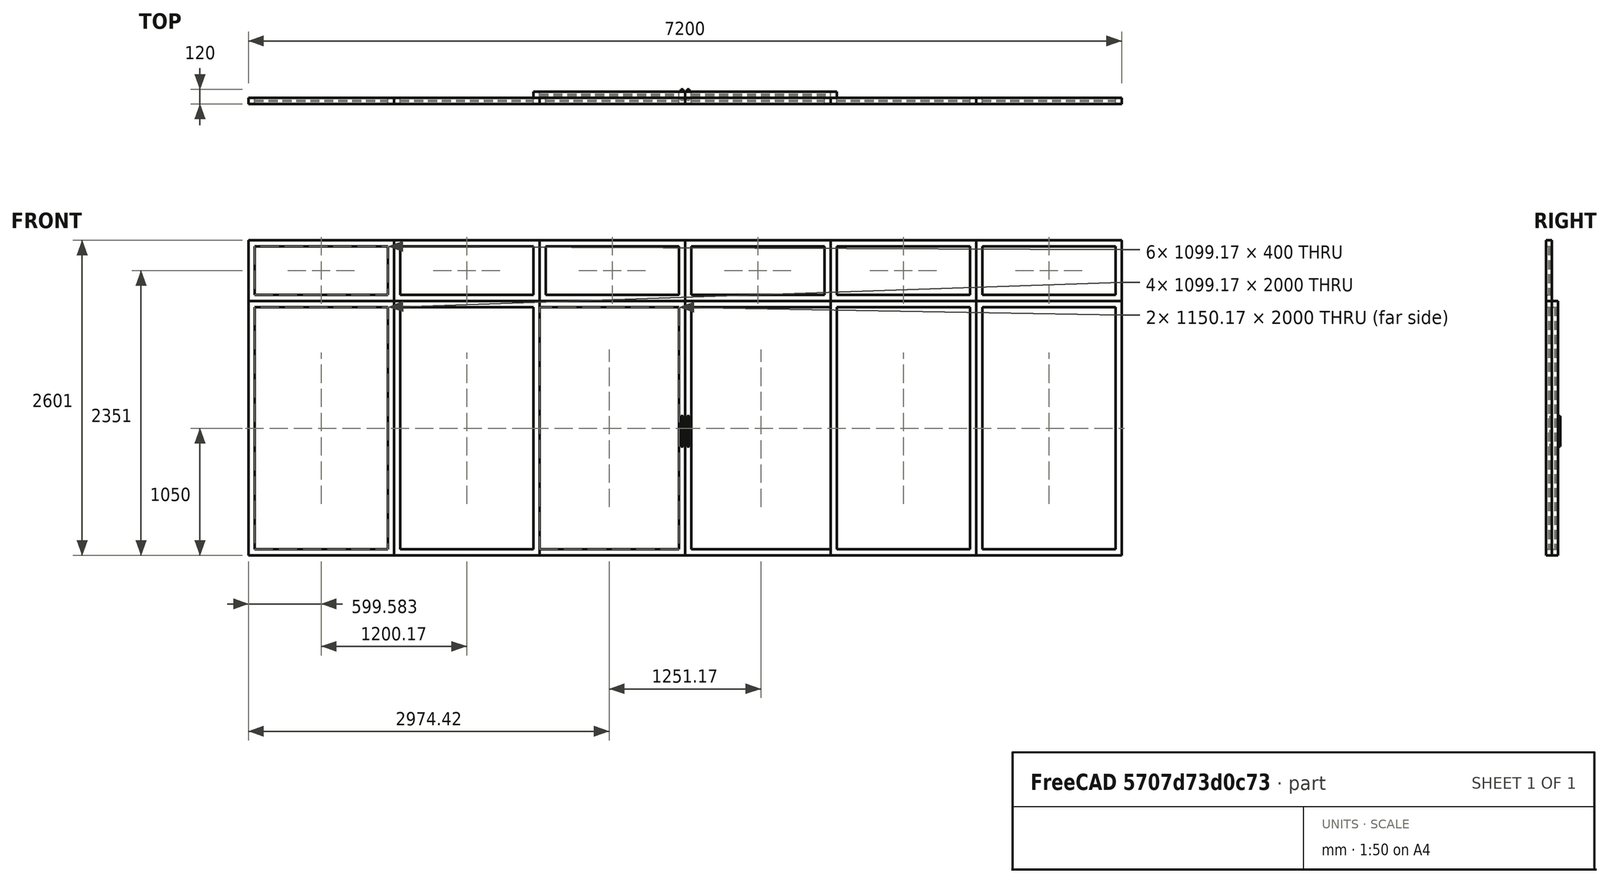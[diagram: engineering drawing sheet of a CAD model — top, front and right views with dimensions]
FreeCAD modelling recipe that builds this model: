
FCSTD DOCUMENT  (FreeCAD 0.16R6704 (Git))
Label: 6 frame modules with doors
License: CreativeCommons Attribution
LicenseURL: http://creativecommons.org/licenses/by/4.0/
objects: Sketcher::SketchObject×1, Part::FeaturePython×1
note: 2 computed .brp shape members not serialized (recipe doc carries the construction recipe); baked Part::Feature solids carry a one-line shape summary decoded from their .brp

FEATURE [Sketcher::SketchObject] Sketch190
  Placement = pos=(0,0,0) rot=(1,0,0;1.5708rad)
  sketch-geometry (135):
    g0: LineSegment StartX=-2 StartY=-2 StartZ=0 EndX=7202 EndY=-2 EndZ=0
    g1: LineSegment StartX=7202 StartY=-2 StartZ=0 EndX=7202 EndY=2603 EndZ=0
    g2: LineSegment StartX=7202 StartY=2603 StartZ=0 EndX=-2 EndY=2603 EndZ=0
    g3: LineSegment StartX=-2 StartY=2603 StartZ=0 EndX=-2 EndY=-2 EndZ=0
    g4: LineSegment StartX=0 StartY=2601 StartZ=0 EndX=1199.17 EndY=2601 EndZ=0
    g5: LineSegment StartX=1199.17 StartY=2601 StartZ=0 EndX=1199.17 EndY=2101 EndZ=0
    g6: LineSegment StartX=1199.17 StartY=2101 StartZ=0 EndX=0 EndY=2101 EndZ=0
    g7: LineSegment StartX=0 StartY=2101 StartZ=0 EndX=0 EndY=2601 EndZ=0
    g8: LineSegment StartX=50 StartY=2551 StartZ=0 EndX=1149.17 EndY=2551 EndZ=0
    g9: LineSegment StartX=1149.17 StartY=2551 StartZ=0 EndX=1149.17 EndY=2151 EndZ=0
    g10: LineSegment StartX=1149.17 StartY=2151 StartZ=0 EndX=50 EndY=2151 EndZ=0
    g11: LineSegment StartX=50 StartY=2151 StartZ=0 EndX=50 EndY=2551 EndZ=0
    g12: LineSegment StartX=0 StartY=2100 StartZ=0 EndX=1199.17 EndY=2100 EndZ=0
    g13: LineSegment StartX=1199.17 StartY=2100 StartZ=0 EndX=1199.17 EndY=0 EndZ=0
    g14: LineSegment StartX=1199.17 StartY=0 StartZ=0 EndX=0 EndY=0 EndZ=0
    g15: LineSegment StartX=0 StartY=0 StartZ=0 EndX=0 EndY=2100 EndZ=0
    g16: LineSegment StartX=50 StartY=2050 StartZ=0 EndX=1149.17 EndY=2050 EndZ=0
    g17: LineSegment StartX=1149.17 StartY=2050 StartZ=0 EndX=1149.17 EndY=50 EndZ=0
    g18: LineSegment StartX=1149.17 StartY=50 StartZ=0 EndX=50 EndY=50 EndZ=0
    g19: LineSegment StartX=50 StartY=50 StartZ=0 EndX=50 EndY=2050 EndZ=0
    g20: LineSegment StartX=-1 StartY=2602 StartZ=0 EndX=7201 EndY=2602 EndZ=0
    g21: LineSegment StartX=7201 StartY=2602 StartZ=0 EndX=7201 EndY=-1 EndZ=0
    g22: LineSegment StartX=7201 StartY=-1 StartZ=0 EndX=-1 EndY=-1 EndZ=0
    g23: LineSegment StartX=-1 StartY=-1 StartZ=0 EndX=-1 EndY=2602 EndZ=0
    g24: LineSegment StartX=1200.17 StartY=2601 StartZ=0 EndX=2399.33 EndY=2601 EndZ=0
    g25: LineSegment StartX=2399.33 StartY=2601 StartZ=0 EndX=2399.33 EndY=2101 EndZ=0
    g26: LineSegment StartX=2399.33 StartY=2101 StartZ=0 EndX=1200.17 EndY=2101 EndZ=0
    g27: LineSegment StartX=1200.17 StartY=2101 StartZ=0 EndX=1200.17 EndY=2601 EndZ=0
    g28: LineSegment StartX=1250.17 StartY=2551 StartZ=0 EndX=2349.33 EndY=2551 EndZ=0
    g29: LineSegment StartX=2349.33 StartY=2551 StartZ=0 EndX=2349.33 EndY=2151 EndZ=0
    g30: LineSegment StartX=2349.33 StartY=2151 StartZ=0 EndX=1250.17 EndY=2151 EndZ=0
    g31: LineSegment StartX=1250.17 StartY=2151 StartZ=0 EndX=1250.17 EndY=2551 EndZ=0
    g32: LineSegment StartX=1200.17 StartY=2100 StartZ=0 EndX=2399.33 EndY=2100 EndZ=0
    g33: LineSegment StartX=2399.33 StartY=2100 StartZ=0 EndX=2399.33 EndY=0 EndZ=0
    g34: LineSegment StartX=2399.33 StartY=0 StartZ=0 EndX=1200.17 EndY=0 EndZ=0
    g35: LineSegment StartX=1200.17 StartY=0 StartZ=0 EndX=1200.17 EndY=2100 EndZ=0
    g36: LineSegment StartX=1250.17 StartY=2050 StartZ=0 EndX=2349.33 EndY=2050 EndZ=0
    g37: LineSegment StartX=2349.33 StartY=2050 StartZ=0 EndX=2349.33 EndY=50 EndZ=0
    g38: LineSegment StartX=2349.33 StartY=50 StartZ=0 EndX=1250.17 EndY=50 EndZ=0
    g39: LineSegment StartX=1250.17 StartY=50 StartZ=0 EndX=1250.17 EndY=2050 EndZ=0
    g40: LineSegment [constr] StartX=0 StartY=2601 StartZ=0 EndX=1200.17 EndY=2601 EndZ=0
    g41: LineSegment StartX=2400.33 StartY=2601 StartZ=0 EndX=3599.5 EndY=2601 EndZ=0
    g42: LineSegment StartX=3599.5 StartY=2601 StartZ=0 EndX=3599.5 EndY=2101 EndZ=0
    g43: LineSegment StartX=3599.5 StartY=2101 StartZ=0 EndX=2400.33 EndY=2101 EndZ=0
    g44: LineSegment StartX=2400.33 StartY=2101 StartZ=0 EndX=2400.33 EndY=2601 EndZ=0
    g45: LineSegment StartX=2450.33 StartY=2551 StartZ=0 EndX=3549.5 EndY=2551 EndZ=0
    g46: LineSegment StartX=3549.5 StartY=2551 StartZ=0 EndX=3549.5 EndY=2151 EndZ=0
    g47: LineSegment StartX=3549.5 StartY=2151 StartZ=0 EndX=2450.33 EndY=2151 EndZ=0
    g48: LineSegment StartX=2450.33 StartY=2151 StartZ=0 EndX=2450.33 EndY=2551 EndZ=0
    g49: LineSegment StartX=2349.33 StartY=2100 StartZ=0 EndX=3599.5 EndY=2100 EndZ=0
    g50: LineSegment StartX=3599.5 StartY=2100 StartZ=0 EndX=3599.5 EndY=0 EndZ=0
    g51: LineSegment StartX=3599.5 StartY=0 StartZ=0 EndX=2349.33 EndY=0 EndZ=0
    g52: LineSegment StartX=2349.33 StartY=0 StartZ=0 EndX=2349.33 EndY=2100 EndZ=0
    g53: LineSegment StartX=2399.33 StartY=2050 StartZ=0 EndX=3549.5 EndY=2050 EndZ=0
    g54: LineSegment StartX=3549.5 StartY=2050 StartZ=0 EndX=3549.5 EndY=50 EndZ=0
    g55: LineSegment StartX=3549.5 StartY=50 StartZ=0 EndX=2399.33 EndY=50 EndZ=0
    g56: LineSegment StartX=2399.33 StartY=50 StartZ=0 EndX=2399.33 EndY=2050 EndZ=0
    g57: LineSegment [constr] StartX=1200.17 StartY=2601 StartZ=0 EndX=2400.33 EndY=2601 EndZ=0
    g58: LineSegment StartX=3600.5 StartY=2601 StartZ=0 EndX=4799.67 EndY=2601 EndZ=0
    g59: LineSegment StartX=4799.67 StartY=2601 StartZ=0 EndX=4799.67 EndY=2101 EndZ=0
    g60: LineSegment StartX=4799.67 StartY=2101 StartZ=0 EndX=3600.5 EndY=2101 EndZ=0
    g61: LineSegment StartX=3600.5 StartY=2101 StartZ=0 EndX=3600.5 EndY=2601 EndZ=0
    g62: LineSegment StartX=3650.5 StartY=2551 StartZ=0 EndX=4749.67 EndY=2551 EndZ=0
    g63: LineSegment StartX=4749.67 StartY=2551 StartZ=0 EndX=4749.67 EndY=2151 EndZ=0
    g64: LineSegment StartX=4749.67 StartY=2151 StartZ=0 EndX=3650.5 EndY=2151 EndZ=0
    g65: LineSegment StartX=3650.5 StartY=2151 StartZ=0 EndX=3650.5 EndY=2551 EndZ=0
    g66: LineSegment StartX=3600.5 StartY=2100 StartZ=0 EndX=4850.67 EndY=2100 EndZ=0
    g67: LineSegment StartX=4850.67 StartY=2100 StartZ=0 EndX=4850.67 EndY=0 EndZ=0
    g68: LineSegment StartX=4850.67 StartY=0 StartZ=0 EndX=3600.5 EndY=0 EndZ=0
    g69: LineSegment StartX=3600.5 StartY=0 StartZ=0 EndX=3600.5 EndY=2100 EndZ=0
    g70: LineSegment StartX=3650.5 StartY=2050 StartZ=0 EndX=4800.67 EndY=2050 EndZ=0
    g71: LineSegment StartX=4800.67 StartY=2050 StartZ=0 EndX=4800.67 EndY=50 EndZ=0
    g72: LineSegment StartX=4800.67 StartY=50 StartZ=0 EndX=3650.5 EndY=50 EndZ=0
    g73: LineSegment StartX=3650.5 StartY=50 StartZ=0 EndX=3650.5 EndY=2050 EndZ=0
    g74: LineSegment [constr] StartX=2400.33 StartY=2601 StartZ=0 EndX=3600.5 EndY=2601 EndZ=0
    g75: LineSegment StartX=4800.67 StartY=2601 StartZ=0 EndX=5999.83 EndY=2601 EndZ=0
    g76: LineSegment StartX=5999.83 StartY=2601 StartZ=0 EndX=5999.83 EndY=2101 EndZ=0
    g77: LineSegment StartX=5999.83 StartY=2101 StartZ=0 EndX=4800.67 EndY=2101 EndZ=0
    g78: LineSegment StartX=4800.67 StartY=2101 StartZ=0 EndX=4800.67 EndY=2601 EndZ=0
    g79: LineSegment StartX=4850.67 StartY=2551 StartZ=0 EndX=5949.83 EndY=2551 EndZ=0
    g80: LineSegment StartX=5949.83 StartY=2551 StartZ=0 EndX=5949.83 EndY=2151 EndZ=0
    g81: LineSegment StartX=5949.83 StartY=2151 StartZ=0 EndX=4850.67 EndY=2151 EndZ=0
    g82: LineSegment StartX=4850.67 StartY=2151 StartZ=0 EndX=4850.67 EndY=2551 EndZ=0
    g83: LineSegment StartX=4800.67 StartY=2100 StartZ=0 EndX=5999.83 EndY=2100 EndZ=0
    g84: LineSegment StartX=5999.83 StartY=2100 StartZ=0 EndX=5999.83 EndY=0 EndZ=0
    g85: LineSegment StartX=5999.83 StartY=0 StartZ=0 EndX=4800.67 EndY=0 EndZ=0
    g86: LineSegment StartX=4800.67 StartY=0 StartZ=0 EndX=4800.67 EndY=2100 EndZ=0
    g87: LineSegment StartX=4850.67 StartY=2050 StartZ=0 EndX=5949.83 EndY=2050 EndZ=0
    g88: LineSegment StartX=5949.83 StartY=2050 StartZ=0 EndX=5949.83 EndY=50 EndZ=0
    g89: LineSegment StartX=5949.83 StartY=50 StartZ=0 EndX=4850.67 EndY=50 EndZ=0
    g90: LineSegment StartX=4850.67 StartY=50 StartZ=0 EndX=4850.67 EndY=2050 EndZ=0
    g91: LineSegment [constr] StartX=3600.5 StartY=2601 StartZ=0 EndX=4800.67 EndY=2601 EndZ=0
    g92: LineSegment StartX=6000.83 StartY=2601 StartZ=0 EndX=7200 EndY=2601 EndZ=0
    g93: LineSegment StartX=7200 StartY=2601 StartZ=0 EndX=7200 EndY=2101 EndZ=0
    g94: LineSegment StartX=7200 StartY=2101 StartZ=0 EndX=6000.83 EndY=2101 EndZ=0
    g95: LineSegment StartX=6000.83 StartY=2101 StartZ=0 EndX=6000.83 EndY=2601 EndZ=0
    g96: LineSegment StartX=6050.83 StartY=2551 StartZ=0 EndX=7150 EndY=2551 EndZ=0
    g97: LineSegment StartX=7150 StartY=2551 StartZ=0 EndX=7150 EndY=2151 EndZ=0
    g98: LineSegment StartX=7150 StartY=2151 StartZ=0 EndX=6050.83 EndY=2151 EndZ=0
    g99: LineSegment StartX=6050.83 StartY=2151 StartZ=0 EndX=6050.83 EndY=2551 EndZ=0
    g100: LineSegment StartX=6000.83 StartY=2100 StartZ=0 EndX=7200 EndY=2100 EndZ=0
    g101: LineSegment StartX=7200 StartY=2100 StartZ=0 EndX=7200 EndY=0 EndZ=0
    g102: LineSegment StartX=7200 StartY=0 StartZ=0 EndX=6000.83 EndY=0 EndZ=0
    g103: LineSegment StartX=6000.83 StartY=0 StartZ=0 EndX=6000.83 EndY=2100 EndZ=0
    g104: LineSegment StartX=6050.83 StartY=2050 StartZ=0 EndX=7150 EndY=2050 EndZ=0
    g105: LineSegment StartX=7150 StartY=2050 StartZ=0 EndX=7150 EndY=50 EndZ=0
    g106: LineSegment StartX=7150 StartY=50 StartZ=0 EndX=6050.83 EndY=50 EndZ=0
    g107: LineSegment StartX=6050.83 StartY=50 StartZ=0 EndX=6050.83 EndY=2050 EndZ=0
    g108: LineSegment [constr] StartX=4800.67 StartY=2601 StartZ=0 EndX=6000.83 EndY=2601 EndZ=0
    g109: LineSegment StartX=3564.5 StartY=1150 StartZ=0 EndX=3584.5 EndY=1150 EndZ=0
    g110: LineSegment StartX=3584.5 StartY=1150 StartZ=0 EndX=3584.5 EndY=900 EndZ=0
    g111: LineSegment StartX=3584.5 StartY=900 StartZ=0 EndX=3564.5 EndY=900 EndZ=0
    g112: LineSegment StartX=3564.5 StartY=900 StartZ=0 EndX=3564.5 EndY=1150 EndZ=0
    g113: LineSegment StartX=3615.5 StartY=1150 StartZ=0 EndX=3635.5 EndY=1150 EndZ=0
    g114: LineSegment StartX=3635.5 StartY=1150 StartZ=0 EndX=3635.5 EndY=900 EndZ=0
    g115: LineSegment StartX=3635.5 StartY=900 StartZ=0 EndX=3615.5 EndY=900 EndZ=0
    g116: LineSegment StartX=3615.5 StartY=900 StartZ=0 EndX=3615.5 EndY=1150 EndZ=0
    g117: LineSegment [constr] StartX=60.6664 StartY=50 StartZ=0 EndX=60.6664 EndY=0 EndZ=0
    g118: LineSegment [constr] StartX=0 StartY=2393.34 StartZ=0 EndX=50 EndY=2393.34 EndZ=0
    g119: LineSegment [constr] StartX=141.741 StartY=2601 StartZ=0 EndX=141.741 EndY=2551 EndZ=0
    g120: LineSegment [constr] StartX=1149.17 StartY=2527.5 StartZ=0 EndX=1199.17 EndY=2527.5 EndZ=0
    g121: LineSegment [constr] StartX=1200.17 StartY=2516.49 StartZ=0 EndX=1250.17 EndY=2516.49 EndZ=0
    g122: LineSegment [constr] StartX=2349.33 StartY=2495 StartZ=0 EndX=2399.33 EndY=2495 EndZ=0
    g123: LineSegment [constr] StartX=2400.33 StartY=2493.39 StartZ=0 EndX=2450.33 EndY=2493.39 EndZ=0
    g124: LineSegment [constr] StartX=3549.5 StartY=2542 StartZ=0 EndX=3599.5 EndY=2542 EndZ=0
    g125: LineSegment [constr] StartX=3600.5 StartY=2538 StartZ=0 EndX=3650.5 EndY=2538 EndZ=0
    g126: LineSegment [constr] StartX=4749.67 StartY=2530.45 StartZ=0 EndX=4799.67 EndY=2530.45 EndZ=0
    g127: LineSegment [constr] StartX=4800.67 StartY=2534.58 StartZ=0 EndX=4850.67 EndY=2534.58 EndZ=0
    g128: LineSegment [constr] StartX=5949.83 StartY=2532.69 StartZ=0 EndX=5999.83 EndY=2532.69 EndZ=0
    g129: LineSegment [constr] StartX=6000.83 StartY=2528 StartZ=0 EndX=6050.83 EndY=2528 EndZ=0
    g130: LineSegment [constr] StartX=7150 StartY=2521.34 StartZ=0 EndX=7200 EndY=2521.34 EndZ=0
    g131: LineSegment [constr] StartX=28.9872 StartY=2151 StartZ=0 EndX=28.9872 EndY=2101 EndZ=0
    g132: LineSegment [constr] StartX=57.4326 StartY=2100 StartZ=0 EndX=57.4326 EndY=2050 EndZ=0
    g133: LineSegment [constr] StartX=3584.5 StartY=1150 StartZ=0 EndX=3599.5 EndY=1150 EndZ=0
    g134: LineSegment [constr] StartX=3615.5 StartY=1150 StartZ=0 EndX=3600.5 EndY=1150 EndZ=0
  constraints (399):
    c: Coincident(g0,g1)
    c: Coincident(g1,g2)
    c: Coincident(g2,g3)
    c: Coincident(g3,g0)
    c: Horizontal(g0)
    c: Horizontal(g2)
    c: Vertical(g1)
    c: Vertical(g3)
    c: Coincident(g4,g5)
    c: Coincident(g5,g6)
    c: Coincident(g6,g7)
    c: Coincident(g7,g4)
    c: Horizontal(g4)
    c: Horizontal(g6)
    c: Vertical(g5)
    c: Vertical(g7)
    c: Coincident(g8,g9)
    c: Coincident(g9,g10)
    c: Coincident(g10,g11)
    c: Coincident(g11,g8)
    c: Horizontal(g8)
    c: Horizontal(g10)
    c: Vertical(g9)
    c: Vertical(g11)
    c: Coincident(g12,g13)
    c: Coincident(g13,g14)
    c: Coincident(g14,g15)
    c: Coincident(g15,g12)
    c: Horizontal(g12)
    c: Horizontal(g14)
    c: Vertical(g13)
    c: Vertical(g15)
    c: Coincident(g16,g17)
    c: Coincident(g17,g18)
    c: Coincident(g18,g19)
    c: Coincident(g19,g16)
    c: Horizontal(g16)
    c: Horizontal(g18)
    c: Vertical(g17)
    c: Vertical(g19)
    c: Coincident(g20,g21)
    c: Coincident(g21,g22)
    c: Coincident(g22,g23)
    c: Coincident(g23,g20)
    c: Horizontal(g20)
    c: Horizontal(g22)
    c: Vertical(g21)
    c: Vertical(g23)
    c: DistanceX(g2,g20) = 1  'Largura do marco vertical 1 geral'
    c: DistanceY(g20,g2) = 1  'Altura do marco geral'
    c: DistanceX(g20,g4) = 1
    c: DistanceY(g4,g20) = 1
    c: DistanceX(g22,g14) = 1
    c: DistanceY(g22,g14) = 1
    c: DistanceY(g12,g6) = 1
    c: DistanceX(g4,g8) = 50  'Dimensão perfis'
    c: Coincident(g14,g-1)  'Constraint58'
    c: DistanceY(g-1,g12) = 2100  'Altura portas e perfis'
    c: DistanceY(g6,g4) = 500  'Altura bandeira'
    c: Coincident(g24,g25)  'Constraint60'
    c: Coincident(g25,g26)
    c: Coincident(g26,g27)
    c: Coincident(g27,g24)
    c: Horizontal(g24)
    c: Horizontal(g26)
    c: Vertical(g25)
    c: Vertical(g27)
    c: Coincident(g28,g29)
    c: Coincident(g29,g30)
    c: Coincident(g30,g31)
    c: Coincident(g31,g28)
    c: Horizontal(g28)
    c: Horizontal(g30)
    c: Vertical(g29)
    c: Vertical(g31)
    c: Coincident(g32,g33)
    c: Coincident(g33,g34)
    c: Coincident(g34,g35)
    c: Coincident(g35,g32)
    c: Horizontal(g32)
    c: Horizontal(g34)
    c: Vertical(g33)
    c: Vertical(g35)
    c: Coincident(g36,g37)
    c: Coincident(g37,g38)
    c: Coincident(g38,g39)
    c: Coincident(g39,g36)
    c: Horizontal(g36)
    c: Horizontal(g38)
    c: Vertical(g37)
    c: Vertical(g39)
    c: Equal(g4,g24) = 1199
    c: Coincident(g4,g40)
    c: Coincident(g24,g40)
    c: Angle(g40) = 0
    c: Coincident(g41,g42)
    c: Coincident(g42,g43)
    c: Coincident(g43,g44)
    c: Coincident(g44,g41)
    c: Horizontal(g41)
    c: Horizontal(g43)
    c: Vertical(g42)
    c: Vertical(g44)
    c: Coincident(g45,g46)
    c: Coincident(g46,g47)
    c: Coincident(g47,g48)
    c: Coincident(g48,g45)
    c: Horizontal(g45)
    c: Horizontal(g47)
    c: Vertical(g46)
    c: Vertical(g48)
    c: Coincident(g49,g50)
    c: Coincident(g50,g51)
    c: Coincident(g51,g52)
    c: Coincident(g52,g49)
    c: Horizontal(g49)
    c: Horizontal(g51)
    c: Vertical(g50)
    c: Vertical(g52)
    c: Coincident(g53,g54)
    c: Coincident(g54,g55)
    c: Coincident(g55,g56)
    c: Coincident(g56,g53)
    c: Horizontal(g53)
    c: Horizontal(g55)
    c: Vertical(g54)
    c: Vertical(g56)
    c: Equal(g4,g41) = 1199
    c: Coincident(g24,g57)
    c: Coincident(g41,g57)
    c: Equal(g40,g57)
    c: Parallel(g57,g40)
    c: Coincident(g58,g59)
    c: Coincident(g59,g60)
    c: Coincident(g60,g61)
    c: Coincident(g61,g58)
    c: Horizontal(g58)
    c: Horizontal(g60)
    c: Vertical(g59)
    c: Vertical(g61)
    c: Coincident(g62,g63)
    c: Coincident(g63,g64)
    c: Coincident(g64,g65)
    c: Coincident(g65,g62)
    c: Horizontal(g62)
    c: Horizontal(g64)
    c: Vertical(g63)
    c: Vertical(g65)
    c: Coincident(g66,g67)
    c: Coincident(g67,g68)
    c: Coincident(g68,g69)
    c: Coincident(g69,g66)
    c: Horizontal(g66)
    c: Horizontal(g68)
    c: Vertical(g67)
    c: Vertical(g69)
    c: Coincident(g70,g71)
    c: Coincident(g71,g72)
    c: Coincident(g72,g73)
    c: Coincident(g73,g70)
    c: Horizontal(g70)
    c: Horizontal(g72)
    c: Vertical(g71)
    c: Vertical(g73)
    c: Equal(g4,g58) = 1199
    c: Coincident(g41,g74)
    c: Coincident(g58,g74)
    c: Equal(g40,g74)
    c: Parallel(g74,g40)
    c: Coincident(g75,g76)
    c: Coincident(g76,g77)
    c: Coincident(g77,g78)
    c: Coincident(g78,g75)
    c: Horizontal(g75)
    c: Horizontal(g77)
    c: Vertical(g76)
    c: Vertical(g78)
    c: Coincident(g79,g80)
    c: Coincident(g80,g81)
    c: Coincident(g81,g82)
    c: Coincident(g82,g79)
    c: Horizontal(g79)
    c: Horizontal(g81)
    c: Vertical(g80)
    c: Vertical(g82)
    c: Coincident(g83,g84)
    c: Coincident(g84,g85)
    c: Coincident(g85,g86)
    c: Coincident(g86,g83)
    c: Horizontal(g83)
    c: Horizontal(g85)
    c: Vertical(g84)
    c: Vertical(g86)
    c: Coincident(g87,g88)
    c: Coincident(g88,g89)
    c: Coincident(g89,g90)
    c: Coincident(g90,g87)
    c: Horizontal(g87)
    c: Horizontal(g89)
    c: Vertical(g88)
    c: Vertical(g90)
    c: Equal(g4,g75) = 1199
    c: Coincident(g58,g91)
    c: Coincident(g75,g91)
    c: Equal(g40,g91)
    c: Parallel(g91,g40)
    c: Coincident(g92,g93)
    c: Coincident(g93,g94)
    c: Coincident(g94,g95)
    c: Coincident(g95,g92)
    c: Horizontal(g92)
    c: Horizontal(g94)
    c: Vertical(g93)
    c: Vertical(g95)
    c: Coincident(g96,g97)
    c: Coincident(g97,g98)
    c: Coincident(g98,g99)
    c: Coincident(g99,g96)
    c: Horizontal(g96)
    c: Horizontal(g98)
    c: Vertical(g97)
    c: Vertical(g99)
    c: Coincident(g100,g101)
    c: Coincident(g101,g102)
    c: Coincident(g102,g103)
    c: Coincident(g103,g100)
    c: Horizontal(g100)
    c: Horizontal(g102)
    c: Vertical(g101)
    c: Vertical(g103)
    c: Coincident(g104,g105)
    c: Coincident(g105,g106)
    c: Coincident(g106,g107)
    c: Coincident(g107,g104)
    c: Horizontal(g104)
    c: Horizontal(g106)
    c: Vertical(g105)
    c: Vertical(g107)
    c: Equal(g4,g92) = 1199
    c: Coincident(g75,g108)
    c: Coincident(g92,g108)
    c: Equal(g40,g108)
    c: Parallel(g108,g40)
    c: Coincident(g109,g110)
    c: Coincident(g110,g111)
    c: Coincident(g111,g112)
    c: Coincident(g112,g109)
    c: Horizontal(g109)
    c: Horizontal(g111)
    c: Vertical(g110)
    c: Vertical(g112)
    c: Coincident(g113,g114)
    c: Coincident(g114,g115)
    c: Coincident(g115,g116)
    c: Coincident(g116,g113)
    c: Horizontal(g113)
    c: Horizontal(g115)
    c: Vertical(g114)
    c: Vertical(g116)
    c: DistanceY(g110,g115) = 0
    c: DistanceY(g113,g109) = 0
    c: DistanceX(g109,g109) = 20  'Largura puxadores'
    c: DistanceX(g26,g32) = 0  'Constraint263'
    c: DistanceX(g36,g29) = 0
    c: DistanceX(g36,g49) = 0
    c: DistanceX(g42,g49) = 0
    c: DistanceX(g60,g66) = 0
    c: DistanceX(g87,g81) = 0
    c: DistanceX(g66,g87) = 0
    c: DistanceX(g76,g83) = 0
    c: DistanceX(g94,g100) = 0
    c: DistanceX(g93,g100) = 0
    c: DistanceX(g-1,g101) = 7200  'Largura do vão'
    c: DistanceY(g8,g28) = 0  'Constraint280'
    c: DistanceY(g28,g45) = 0  'Constraint278'
    c: DistanceY(g45,g62) = 0  'Constraint277'
    c: DistanceY(g62,g79) = 0
    c: DistanceY(g79,g96) = 0
    c: DistanceX(g92,g20) = 1
    c: DistanceX(g20,g1) = 1  'Largura marco geral vertical 2'
    c: DistanceX(g97,g104) = 0
    c: DistanceY(g106,g88) = 0
    c: DistanceY(g84,g102) = 0
    c: DistanceY(g71,g89) = 0
    c: DistanceY(g67,g85) = 0
    c: DistanceY(g54,g72) = 0
    c: DistanceY(g68,g50) = 0
    c: DistanceY(g55,g37) = 0
    c: DistanceY(g51,g33) = 0
    c: DistanceY(g38,g17) = 0
    c: DistanceY(g34,g13) = 0
    c: PointOnObject(g117,g18)
    c: PointOnObject(g117,g14)
    c: PointOnObject(g118,g7)
    c: PointOnObject(g118,g11)
    c: DistanceX(g10,g16) = 0
    c: PointOnObject(g119,g4)
    c: PointOnObject(g119,g8)
    c: DistanceX(g4,g24) = 1
    c: PointOnObject(g120,g9)
    c: PointOnObject(g120,g5)
    c: PointOnObject(g121,g27)
    c: PointOnObject(g121,g31)
    c: DistanceY(g9,g30) = 0
    c: DistanceX(g16,g9) = 0
    c: DistanceX(g30,g36) = 0
    c: DistanceY(g16,g36) = 0
    c: DistanceX(g5,g12) = 0
    c: DistanceY(g5,g26) = 0
    c: DistanceY(g12,g32) = 0
    c: PointOnObject(g122,g29)
    c: PointOnObject(g122,g25)
    c: PointOnObject(g123,g44)
    c: PointOnObject(g123,g48)
    c: DistanceY(g29,g47) = 0
    c: DistanceY(g25,g43) = 0
    c: DistanceY(g49,g32) = 0
    c: DistanceX(g25,g32) = 0
    c: DistanceY(g36,g53) = 0
    c: PointOnObject(g124,g46)
    c: PointOnObject(g124,g42)
    c: PointOnObject(g125,g61)
    c: PointOnObject(g125,g65)
    c: DistanceY(g46,g64) = 0
    c: DistanceX(g53,g46) = 0
    c: DistanceX(g64,g70) = 0
    c: DistanceY(g53,g70) = 0
    c: DistanceY(g42,g60) = 0
    c: DistanceY(g49,g66) = 0
    c: PointOnObject(g126,g63)
    c: PointOnObject(g126,g59)
    c: PointOnObject(g127,g78)
    c: PointOnObject(g127,g82)
    c: DistanceY(g63,g81) = 0
    c: DistanceY(g59,g77) = 0
    c: DistanceX(g77,g83) = 0
    c: DistanceX(g83,g70) = 0
    c: DistanceY(g70,g87) = 0
    c: PointOnObject(g128,g80)
    c: PointOnObject(g128,g76)
    c: PointOnObject(g129,g95)
    c: PointOnObject(g129,g99)
    c: DistanceY(g80,g98) = 0
    c: DistanceX(g87,g80) = 0
    c: DistanceX(g98,g104) = 0
    c: DistanceY(g87,g104) = 0
    c: DistanceY(g76,g94) = 0
    c: DistanceY(g83,g100) = 0
    c: PointOnObject(g130,g97)
    c: PointOnObject(g130,g93)
    c: PointOnObject(g131,g10)
    c: PointOnObject(g131,g6)
    c: PointOnObject(g132,g12)
    c: PointOnObject(g132,g16)
    c: Equal(g119,g118)
    c: Equal(g118,g120)
    c: Equal(g120,g121)
    c: Equal(g121,g122)
    c: Equal(g122,g123)
    c: Equal(g123,g124)
    c: Equal(g124,g125)
    c: Equal(g125,g126)
    c: Equal(g126,g127)
    c: Equal(g127,g128)
    c: Equal(g128,g129)
    c: Equal(g129,g130)
    c: Equal(g130,g131)
    c: Equal(g131,g132)
    c: Equal(g132,g117)
    c: DistanceY(g0,g22) = 1  'Altura marco inferior geral'
    c: Equal(g109,g113)  'Constraint386'
    c: DistanceY(g111,g109) = 250  'Altura puxadores'
    c: DistanceY(g-1,g111) = 900  'Altura dos puxadores ao chão'
    c: DistanceY(g83,g66) = 0  'Constraint388'
    c: DistanceX(g109,g50) = 15  'Distância do puxador'
    c: Coincident(g133,g109)  'Constraint389'
    c: PointOnObject(g133,g50)  'Constraint387'
    c: Horizontal(g133)  'Constraint385'
    c: Coincident(g134,g113)  'Constraint384'
    c: Horizontal(g134)  'Constraint383'
    c: Equal(g133,g134)  'Constraint382'
    c: PointOnObject(g134,g69)
    c: DistanceX(g53,g32) = 0
    c: Angle(g119) = -1.5708
    c: Angle(g118) = 0
    c: Angle(g131) = -1.5708
    c: Angle(g132) = -1.5708
    c: Angle(g117) = -1.5708
    c: Angle(g130) = 0
    c: Angle(g120) = 0
    c: Angle(g121) = 0
    c: Angle(g122) = 0
    c: Angle(g123) = 0
    c: Angle(g124) = 0
    c: Angle(g125) = 0
    c: Angle(g126) = 0
    c: Angle(g127) = 0
    c: Angle(g128) = 0
    c: Angle(g129) = 0
FEATURE [Part::FeaturePython] Window120  label="6 frame modules with doors "  # WARN: FeaturePython — macro-defined, semantics opaque (R4)
  Base = -> Sketch190
  Height = 0
  HoleDepth = 0
  MoveWithHost = true
  Normal = (0,1,0)
  Preset = 0
  Role = 0
  Width = 0
  WindowParts = VIDRO1 | Glass panel | Wire2 | 10.0 | 20.0 | SUPORTE 2 | Frame | Wire3,Wire4 | 50.0 | 0.0 | VIDRO 2 | Glass panel | Wire4 | 10.0 | 20.0 | SUPORTE 3 | Frame | Wire6,Wire7 | 50.0 | 0.0 | VIDRO 3 | Glass panel | Wire7 | 10.0 | 20.0 | SUPORTE 4 | Frame | Wire8,Wire9 | 50.0 | 0.0 | VIDRO 4 | Glass panel | Wire9 | 10.0 | 20.0 | SUPORTE 5 | Frame | Wire10,Wire11 | 50.0 | 0.0 | VIDRO 5 | Glass panel | Wire11 | 10.0 | 20.0 | SUPORTE 6 | Frame | Wire12,Wire13 | 50.0 | 50.0 | VIDRO 6 | Glass panel | Wire13 | 10.0 | 70.0 | SUPORTE 7 | Frame | Wire14,Wire15 | 50.0 | 0.0 | VIDRO 7 | Glass panel | Wire15 | 10.0 | 20.0 | SUPORTE 8 | Frame | Wire16,Wire17 | 50.0 | 50.0 | VIDRO 8 | Glass panel | Wire17 | 10.0 | 70.0 | SUPORTE 9 | Solid panel | Wire18,Wire19 | 50.0 | 0.0 | VIDRO 9 | Glass panel | Wire19 | 10.0 | 20.0 | SUPORTE 10 | Frame | Wire20,Wire21 | 50.0 | 0.0 | VIDRO 10 | Glass panel | Wire21 | 10.0 | 20.0 | SUPORTE 11 | Frame | Wire22,Wire23 | 50.0 | 0.0 | VIDRO 11 | Glass panel | Wire23 | 10.0 | 20.0 | SUPORTE 12 | Frame | Wire24,Wire25 | 50.0 | 0.0 | VIDRO 12 | Glass panel | Wire25 | 10.0 | 20.0 | SUPORTE 1 | Frame | Wire1,Wire2 | 50.0 | 0.0 | PUXADOR 1 | Frame | Wire26 | 20.0 | 30.0 | PUXADOR 2 | Frame | Wire27 | 20.0 | 30.0 | PUXADOR 3 | Frame | Wire26 | 20.0 | 100.0 | PUXADOR 4 | Frame | Wire27 | 20.0 | 100.0
